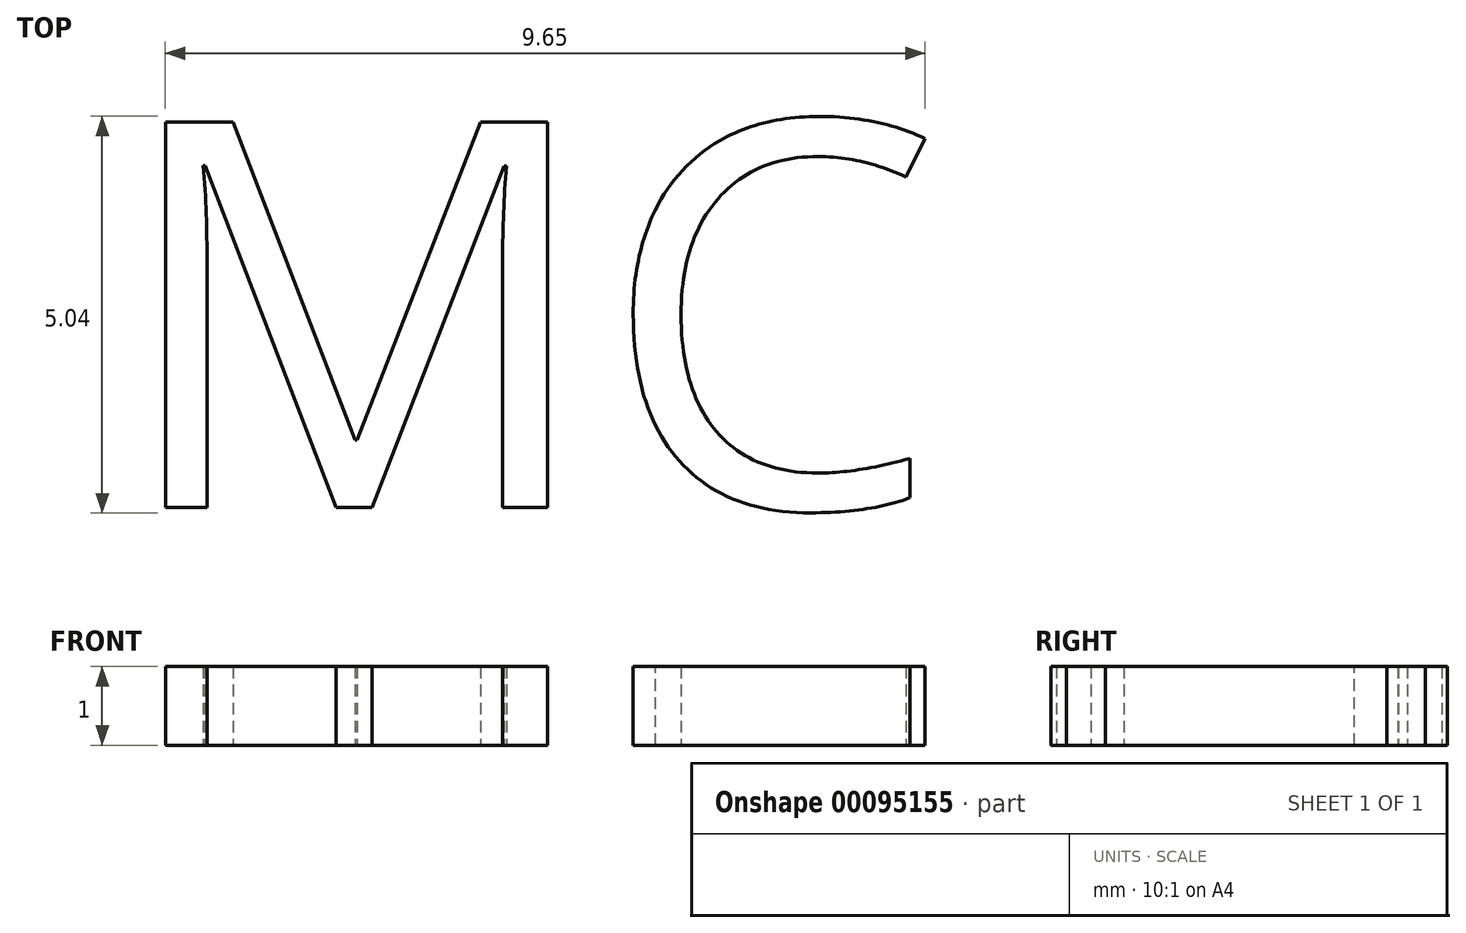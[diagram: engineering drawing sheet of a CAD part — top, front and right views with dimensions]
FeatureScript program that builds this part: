
annotation { "Feature Type Name" : "Feature", "Feature Type Description" : "" }
export const myFeature = defineFeature(function(context is Context, id is Id, definition is map)
    precondition{}
    {
        {
            var Q0;
            Q0=qCreatedBy(makeId("Top.planeOp"),FACE);
            var sketch = newSketch(context, id + "F0", { "sketchPlane" : qUnion([Q0])});
            skText(sketch, "E0", { "text": "MC", "fontName": "OpenSans-Regular.ttf"});
            const initialGuessF0  = {"E0": [-0.00486, -0.0024, 1, 0, 0.00494]};
            skSetInitialGuess(sketch, initialGuessF0);
            skSolve(sketch);
        }
        {
            var Q0;
            Q0 = qSketchRegion(id + "F0", true);
            extrude(context, id + "F1", {"entities" : qUnion([Q0]), "depth" : 1 * mm});
        }
    });
